# Revit family: 1000_Sliding_Window_XXXX_Standard
name_source: partatom
category: Windows
revit_build: Autodesk Revit 2014 (Build: 20130308_1515(x64)
units: mm (PartAtom-declared; Revit-internal decimal feet)

## types (72) — shared parameters
Centered In Wall = Yes
Custom Sash Width Side = 800 mm  [stored 2.62467 ft]
Default Sill Height = 800 mm  [stored 2.62467 ft]
Description = Sliding window, XXXX
Equal Sash Width = Yes
Frame Thickness = 76 mm
Heavy Duty Handle Gap = 26 mm
Limit Sash Height Max = 1800 mm  [stored 5.90551 ft]
Limit Sash Height Min = 300 mm  [stored 0.984252 ft]
Limit Sash Width Max = 1500 mm  [stored 4.92126 ft]
Limit Sash Width Min = 300 mm  [stored 0.984252 ft]
Limit Sash Width Side Min = 300 mm  [stored 0.984252 ft]
Limit Window Height Max = 1857 mm
Limit Window Height Min = 357 mm
Limit Window Width Max = 5941 mm  [stored 19.4915 ft]
Limit Window Width Min = 1141 mm  [stored 3.74344 ft]
Manufacturer = Crealco
Model = 1000
Sash Frame Seal = 2 mm  [stored 0.00656168 ft]
URL = http://www.crealco.co.za
Wall Closure = By host
zero-valued in all types: Custom Frame Offset From Exterior

## per-type parameters (varying)
- 1000SW-1806XXXX-1000Pa: Area Middle Sash Glazing=0.16 m²; Area Side Sash Glazing=0.16 m²; Clearvue SHGC Value=0.498; Clearvue U Value=6.41; Custom Windload=1000 mm  [stored 3.28084 ft]; Custom Window Height=590 mm  [stored 1.9357 ft]; Custom Window Width=1790 mm  [stored 5.8727 ft]; Energy Advantage SHGC Value=0.448; Energy Advantage U Value=5.39; Heavy Duty Handle=No; Heavy Duty Interlocker=No; Height=590 mm  [stored 1.9357 ft]; Intruderprufe LowE SHGC Value=0.415; Intruderprufe LowE U Value=5.34; Intruderprufe SHGC Value=0.474; Intruderprufe U Value=6.29; Is Heavy Duty Handle=0 mm  [stored 0 ft]; Is Heavy Duty Mullion=0 mm  [stored 0 ft]; Limit Sash Width Side Max=625 mm; Max Pane Area=0.16 m²; Sash Height=533 mm; Sash Width Middle=462 mm; Sash Width Sides=462 mm; Standard Interlocker=Yes; Width=1790 mm  [stored 5.8727 ft]; Windload Design=1000 mm  [stored 3.28084 ft]
- 1000SW-2106XXXX-1000Pa: Area Middle Sash Glazing=0.19 m²; Area Side Sash Glazing=0.19 m²; Clearvue SHGC Value=0.515; Clearvue U Value=6.4; Custom Windload=1000 mm  [stored 3.28084 ft]; Custom Window Height=590 mm  [stored 1.9357 ft]; Custom Window Width=2090 mm  [stored 6.85696 ft]; Energy Advantage SHGC Value=0.463; Energy Advantage U Value=5.31; Heavy Duty Handle=No; Heavy Duty Interlocker=No; Height=590 mm  [stored 1.9357 ft]; Intruderprufe LowE SHGC Value=0.428; Intruderprufe LowE U Value=5.26; Intruderprufe SHGC Value=0.49; Intruderprufe U Value=6.29; Is Heavy Duty Handle=0 mm  [stored 0 ft]; Is Heavy Duty Mullion=0 mm  [stored 0 ft]; Limit Sash Width Side Max=775 mm; Max Pane Area=0.19 m²; Sash Height=533 mm; Sash Width Middle=537 mm  [stored 1.76181 ft]; Sash Width Sides=537 mm  [stored 1.76181 ft]; Standard Interlocker=Yes; Width=2090 mm  [stored 6.85696 ft]; Windload Design=1000 mm  [stored 3.28084 ft]
- 1000SW-2406XXXX-1000Pa: Area Middle Sash Glazing=0.22 m²; Area Side Sash Glazing=0.22 m²; Clearvue SHGC Value=0.528; Clearvue U Value=6.39; Custom Windload=1000 mm  [stored 3.28084 ft]; Custom Window Height=590 mm  [stored 1.9357 ft]; Custom Window Width=2390 mm  [stored 7.84121 ft]; Energy Advantage SHGC Value=0.474; Energy Advantage U Value=5.25; Heavy Duty Handle=No; Heavy Duty Interlocker=No; Height=590 mm  [stored 1.9357 ft]; Intruderprufe LowE SHGC Value=0.438; Intruderprufe LowE U Value=5.21; Intruderprufe SHGC Value=0.627; Intruderprufe U Value=5.98; Is Heavy Duty Handle=0 mm  [stored 0 ft]; Is Heavy Duty Mullion=0 mm  [stored 0 ft]; Limit Sash Width Side Max=925 mm; Max Pane Area=0.22 m²; Sash Height=533 mm; Sash Width Middle=612 mm; Sash Width Sides=612 mm; Standard Interlocker=Yes; Width=2390 mm  [stored 7.84121 ft]; Windload Design=1000 mm  [stored 3.28084 ft]
- 1000SW-2706XXXX-1000Pa: Area Middle Sash Glazing=0.25 m²; Area Side Sash Glazing=0.25 m²; Clearvue SHGC Value=0.537; Clearvue U Value=6.39; Custom Windload=1000 mm  [stored 3.28084 ft]; Custom Window Height=590 mm  [stored 1.9357 ft]; Custom Window Width=2690 mm  [stored 8.82546 ft]; Energy Advantage SHGC Value=0.483; Energy Advantage U Value=5.21; Heavy Duty Handle=No; Heavy Duty Interlocker=No; Height=590 mm  [stored 1.9357 ft]; Intruderprufe LowE SHGC Value=0.446; Intruderprufe LowE U Value=5.16; Intruderprufe SHGC Value=0.511; Intruderprufe U Value=6.28; Is Heavy Duty Handle=0 mm  [stored 0 ft]; Is Heavy Duty Mullion=0 mm  [stored 0 ft]; Limit Sash Width Side Max=1075 mm; Max Pane Area=0.25 m²; Sash Height=533 mm; Sash Width Middle=687 mm; Sash Width Sides=687 mm; Standard Interlocker=Yes; Width=2690 mm  [stored 8.82546 ft]; Windload Design=1000 mm  [stored 3.28084 ft]
- 1000SW-3006XXXX-1000Pa: Area Middle Sash Glazing=0.29 m²; Area Side Sash Glazing=0.29 m²; Clearvue SHGC Value=0.545; Clearvue U Value=6.39; Custom Windload=1000 mm  [stored 3.28084 ft]; Custom Window Height=590 mm  [stored 1.9357 ft]; Custom Window Width=2990 mm  [stored 9.80971 ft]; Energy Advantage SHGC Value=0.489; Energy Advantage U Value=5.17; Heavy Duty Handle=No; Heavy Duty Interlocker=No; Height=590 mm  [stored 1.9357 ft]; Intruderprufe LowE SHGC Value=0.452; Intruderprufe LowE U Value=5.13; Intruderprufe SHGC Value=0.518; Intruderprufe U Value=6.27; Is Heavy Duty Handle=0 mm  [stored 0 ft]; Is Heavy Duty Mullion=0 mm  [stored 0 ft]; Limit Sash Width Side Max=1225 mm; Max Pane Area=0.29 m²; Sash Height=533 mm; Sash Width Middle=762 mm; Sash Width Sides=762 mm; Standard Interlocker=Yes; Width=2990 mm  [stored 9.80971 ft]; Windload Design=1000 mm  [stored 3.28084 ft]
- 1000SW-1809XXXX-1000Pa: Area Middle Sash Glazing=0.26 m²; Area Side Sash Glazing=0.26 m²; Clearvue SHGC Value=0.561; Clearvue U Value=6.26; Custom Windload=1000 mm  [stored 3.28084 ft]; Custom Window Height=890 mm  [stored 2.91995 ft]; Custom Window Width=1790 mm  [stored 5.8727 ft]; Energy Advantage SHGC Value=0.504; Energy Advantage U Value=5.11; Heavy Duty Handle=No; Heavy Duty Interlocker=No; Height=890 mm  [stored 2.91995 ft]; Intruderprufe LowE SHGC Value=0.468; Intruderprufe LowE U Value=5.05; Intruderprufe SHGC Value=0.534; Intruderprufe U Value=6.15; Is Heavy Duty Handle=0 mm  [stored 0 ft]; Is Heavy Duty Mullion=0 mm  [stored 0 ft]; Limit Sash Width Side Max=625 mm; Max Pane Area=0.26 m²; Sash Height=833 mm; Sash Width Middle=462 mm; Sash Width Sides=462 mm; Standard Interlocker=Yes; Width=1790 mm  [stored 5.8727 ft]; Windload Design=1000 mm  [stored 3.28084 ft]
- 1000SW-2109XXXX-1000Pa: Area Middle Sash Glazing=0.32 m²; Area Side Sash Glazing=0.32 m²; Clearvue SHGC Value=0.58; Clearvue U Value=6.25; Custom Windload=1000 mm  [stored 3.28084 ft]; Custom Window Height=890 mm  [stored 2.91995 ft]; Custom Window Width=2090 mm  [stored 6.85696 ft]; Energy Advantage SHGC Value=0.521; Energy Advantage U Value=5.02; Heavy Duty Handle=No; Heavy Duty Interlocker=No; Height=890 mm  [stored 2.91995 ft]; Intruderprufe LowE SHGC Value=0.483; Intruderprufe LowE U Value=4.96; Intruderprufe SHGC Value=0.552; Intruderprufe U Value=6.14; Is Heavy Duty Handle=0 mm  [stored 0 ft]; Is Heavy Duty Mullion=0 mm  [stored 0 ft]; Limit Sash Width Side Max=775 mm; Max Pane Area=0.32 m²; Sash Height=833 mm; Sash Width Middle=537 mm  [stored 1.76181 ft]; Sash Width Sides=537 mm  [stored 1.76181 ft]; Standard Interlocker=Yes; Width=2090 mm  [stored 6.85696 ft]; Windload Design=1000 mm  [stored 3.28084 ft]
- 1000SW-2409XXXX-1000Pa: Area Middle Sash Glazing=0.37 m²; Area Side Sash Glazing=0.37 m²; Clearvue SHGC Value=0.595; Clearvue U Value=6.25; Custom Windload=1000 mm  [stored 3.28084 ft]; Custom Window Height=890 mm  [stored 2.91995 ft]; Custom Window Width=2390 mm  [stored 7.84121 ft]; Energy Advantage SHGC Value=0.533; Energy Advantage U Value=4.95; Heavy Duty Handle=No; Heavy Duty Interlocker=No; Height=890 mm  [stored 2.91995 ft]; Intruderprufe LowE SHGC Value=0.494; Intruderprufe LowE U Value=4.89; Intruderprufe SHGC Value=0.565; Intruderprufe U Value=6.13; Is Heavy Duty Handle=0 mm  [stored 0 ft]; Is Heavy Duty Mullion=0 mm  [stored 0 ft]; Limit Sash Width Side Max=925 mm; Max Pane Area=0.37 m²; Sash Height=833 mm; Sash Width Middle=612 mm; Sash Width Sides=612 mm; Standard Interlocker=Yes; Width=2390 mm  [stored 7.84121 ft]; Windload Design=1000 mm  [stored 3.28084 ft]
- 1000SW-2709XXXX-1000Pa: Area Middle Sash Glazing=0.43 m²; Area Side Sash Glazing=0.43 m²; Clearvue SHGC Value=0.606; Clearvue U Value=6.24; Custom Windload=1000 mm  [stored 3.28084 ft]; Custom Window Height=890 mm  [stored 2.91995 ft]; Custom Window Width=2690 mm  [stored 8.82546 ft]; Energy Advantage SHGC Value=0.543; Energy Advantage U Value=4.89; Heavy Duty Handle=No; Heavy Duty Interlocker=No; Height=890 mm  [stored 2.91995 ft]; Intruderprufe LowE SHGC Value=0.503; Intruderprufe LowE U Value=4.84; Intruderprufe SHGC Value=0.576; Intruderprufe U Value=6.12; Is Heavy Duty Handle=0 mm  [stored 0 ft]; Is Heavy Duty Mullion=0 mm  [stored 0 ft]; Limit Sash Width Side Max=1075 mm; Max Pane Area=0.43 m²; Sash Height=833 mm; Sash Width Middle=687 mm; Sash Width Sides=687 mm; Standard Interlocker=Yes; Width=2690 mm  [stored 8.82546 ft]; Windload Design=1000 mm  [stored 3.28084 ft]
- 1000SW-3009XXXX-1000Pa: Area Middle Sash Glazing=0.48 m²; Area Side Sash Glazing=0.48 m²; Clearvue SHGC Value=0.615; Clearvue U Value=6.24; Custom Windload=1000 mm  [stored 3.28084 ft]; Custom Window Height=890 mm  [stored 2.91995 ft]; Custom Window Width=2990 mm  [stored 9.80971 ft]; Energy Advantage SHGC Value=0.551; Energy Advantage U Value=4.85; Heavy Duty Handle=No; Heavy Duty Interlocker=No; Height=890 mm  [stored 2.91995 ft]; Intruderprufe LowE SHGC Value=0.51; Intruderprufe LowE U Value=4.79; Intruderprufe SHGC Value=0.584; Intruderprufe U Value=6.12; Is Heavy Duty Handle=0 mm  [stored 0 ft]; Is Heavy Duty Mullion=0 mm  [stored 0 ft]; Limit Sash Width Side Max=1225 mm; Max Pane Area=0.48 m²; Sash Height=833 mm; Sash Width Middle=762 mm; Sash Width Sides=762 mm; Standard Interlocker=Yes; Width=2990 mm  [stored 9.80971 ft]; Windload Design=1000 mm  [stored 3.28084 ft]
- 1000SW-1812XXXX-1000Pa: Area Middle Sash Glazing=0.37 m²; Area Side Sash Glazing=0.37 m²; Clearvue SHGC Value=0.592; Clearvue U Value=6.19; Custom Windload=1000 mm  [stored 3.28084 ft]; Custom Window Height=1190 mm  [stored 3.9042 ft]; Custom Window Width=1790 mm  [stored 5.8727 ft]; Energy Advantage SHGC Value=0.531; Energy Advantage U Value=4.97; Heavy Duty Handle=No; Heavy Duty Interlocker=No; Height=1190 mm  [stored 3.9042 ft]; Intruderprufe LowE SHGC Value=0.494; Intruderprufe LowE U Value=4.91; Intruderprufe SHGC Value=0.563; Intruderprufe U Value=6.08; Is Heavy Duty Handle=0 mm  [stored 0 ft]; Is Heavy Duty Mullion=0 mm  [stored 0 ft]; Limit Sash Width Side Max=625 mm; Max Pane Area=0.37 m²; Sash Height=1133 mm; Sash Width Middle=462 mm; Sash Width Sides=462 mm; Standard Interlocker=Yes; Width=1790 mm  [stored 5.8727 ft]; Windload Design=1000 mm  [stored 3.28084 ft]
- 1000SW-2112XXXX-1000Pa: Area Middle Sash Glazing=0.45 m²; Area Side Sash Glazing=0.45 m²; Clearvue SHGC Value=0.612; Clearvue U Value=6.8; Custom Windload=1000 mm  [stored 3.28084 ft]; Custom Window Height=1190 mm  [stored 3.9042 ft]; Custom Window Width=2090 mm  [stored 6.85696 ft]; Energy Advantage SHGC Value=0.549; Energy Advantage U Value=4.87; Heavy Duty Handle=No; Heavy Duty Interlocker=No; Height=1190 mm  [stored 3.9042 ft]; Intruderprufe LowE SHGC Value=0.51; Intruderprufe LowE U Value=4.81; Intruderprufe SHGC Value=0.582; Intruderprufe U Value=6.07; Is Heavy Duty Handle=0 mm  [stored 0 ft]; Is Heavy Duty Mullion=0 mm  [stored 0 ft]; Limit Sash Width Side Max=775 mm; Max Pane Area=0.45 m²; Sash Height=1133 mm; Sash Width Middle=537 mm  [stored 1.76181 ft]; Sash Width Sides=537 mm  [stored 1.76181 ft]; Standard Interlocker=Yes; Width=2090 mm  [stored 6.85696 ft]; Windload Design=1000 mm  [stored 3.28084 ft]
- 1000SW-2412XXXX-1000Pa: Area Middle Sash Glazing=0.53 m²; Area Side Sash Glazing=0.53 m²; Clearvue SHGC Value=0.628; Clearvue U Value=6.17; Custom Windload=1000 mm  [stored 3.28084 ft]; Custom Window Height=1190 mm  [stored 3.9042 ft]; Custom Window Width=2390 mm  [stored 7.84121 ft]; Energy Advantage SHGC Value=0.562; Energy Advantage U Value=4.8; Heavy Duty Handle=No; Heavy Duty Interlocker=No; Height=1190 mm  [stored 3.9042 ft]; Intruderprufe LowE SHGC Value=0.522; Intruderprufe LowE U Value=4.73; Intruderprufe SHGC Value=0.596; Intruderprufe U Value=6.06; Is Heavy Duty Handle=0 mm  [stored 0 ft]; Is Heavy Duty Mullion=0 mm  [stored 0 ft]; Limit Sash Width Side Max=925 mm; Max Pane Area=0.53 m²; Sash Height=1133 mm; Sash Width Middle=612 mm; Sash Width Sides=612 mm; Standard Interlocker=Yes; Width=2390 mm  [stored 7.84121 ft]; Windload Design=1000 mm  [stored 3.28084 ft]
- 1000SW-2712XXXX-1000Pa: Area Middle Sash Glazing=0.61 m²; Area Side Sash Glazing=0.61 m²; Clearvue SHGC Value=0.64; Clearvue U Value=6.17; Custom Windload=1000 mm  [stored 3.28084 ft]; Custom Window Height=1190 mm  [stored 3.9042 ft]; Custom Window Width=2690 mm  [stored 8.82546 ft]; Energy Advantage SHGC Value=0.573; Energy Advantage U Value=4.74; Heavy Duty Handle=No; Heavy Duty Interlocker=No; Height=1190 mm  [stored 3.9042 ft]; Intruderprufe LowE SHGC Value=0.532; Intruderprufe LowE U Value=4.68; Intruderprufe SHGC Value=0.607; Intruderprufe U Value=6.05; Is Heavy Duty Handle=0 mm  [stored 0 ft]; Is Heavy Duty Mullion=0 mm  [stored 0 ft]; Limit Sash Width Side Max=1075 mm; Max Pane Area=0.61 m²; Sash Height=1133 mm; Sash Width Middle=687 mm; Sash Width Sides=687 mm; Standard Interlocker=Yes; Width=2690 mm  [stored 8.82546 ft]; Windload Design=1000 mm  [stored 3.28084 ft]
- 1000SW-3012XXXX-1000Pa: Area Middle Sash Glazing=0.68 m²; Area Side Sash Glazing=0.68 m²; Clearvue SHGC Value=0.649; Clearvue U Value=6.16; Custom Windload=1000 mm  [stored 3.28084 ft]; Custom Window Height=1190 mm  [stored 3.9042 ft]; Custom Window Width=2990 mm  [stored 9.80971 ft]; Energy Advantage SHGC Value=0.581; Energy Advantage U Value=4.69; Heavy Duty Handle=No; Heavy Duty Interlocker=No; Height=1190 mm  [stored 3.9042 ft]; Intruderprufe LowE SHGC Value=0.539; Intruderprufe LowE U Value=4.63; Intruderprufe SHGC Value=0.616; Intruderprufe U Value=6.04; Is Heavy Duty Handle=0 mm  [stored 0 ft]; Is Heavy Duty Mullion=0 mm  [stored 0 ft]; Limit Sash Width Side Max=1225 mm; Max Pane Area=0.68 m²; Sash Height=1133 mm; Sash Width Middle=762 mm; Sash Width Sides=762 mm; Standard Interlocker=Yes; Width=2990 mm  [stored 9.80971 ft]; Windload Design=1000 mm  [stored 3.28084 ft]
- 1000SW-1815XXXX-1000Pa: Area Middle Sash Glazing=0.48 m²; Area Side Sash Glazing=0.48 m²; Clearvue SHGC Value=0.611; Clearvue U Value=6.15; Custom Windload=1000 mm  [stored 3.28084 ft]; Custom Window Height=1490 mm  [stored 4.88845 ft]; Custom Window Width=1790 mm  [stored 5.8727 ft]; Energy Advantage SHGC Value=0.548; Energy Advantage U Value=4.89; Heavy Duty Handle=No; Heavy Duty Interlocker=No; Height=1490 mm  [stored 4.88845 ft]; Intruderprufe LowE SHGC Value=0.51; Intruderprufe LowE U Value=4.82; Intruderprufe SHGC Value=0.581; Intruderprufe U Value=6.03; Is Heavy Duty Handle=0 mm  [stored 0 ft]; Is Heavy Duty Mullion=0 mm  [stored 0 ft]; Limit Sash Width Side Max=625 mm; Max Pane Area=0.48 m²; Sash Height=1433 mm; Sash Width Middle=462 mm; Sash Width Sides=462 mm; Standard Interlocker=Yes; Width=1790 mm  [stored 5.8727 ft]; Windload Design=1000 mm  [stored 3.28084 ft]
- 1000SW-2115XXXX-1000Pa: Area Middle Sash Glazing=0.58 m²; Area Side Sash Glazing=0.58 m²; Clearvue SHGC Value=0.632; Clearvue U Value=6.14; Custom Windload=1000 mm  [stored 3.28084 ft]; Custom Window Height=1490 mm  [stored 4.88845 ft]; Custom Window Width=2090 mm  [stored 6.85696 ft]; Energy Advantage SHGC Value=0.566; Energy Advantage U Value=4.78; Heavy Duty Handle=No; Heavy Duty Interlocker=No; Height=1490 mm  [stored 4.88845 ft]; Intruderprufe LowE SHGC Value=0.526; Intruderprufe LowE U Value=4.72; Intruderprufe SHGC Value=0.6; Intruderprufe U Value=6.02; Is Heavy Duty Handle=0 mm  [stored 0 ft]; Is Heavy Duty Mullion=0 mm  [stored 0 ft]; Limit Sash Width Side Max=775 mm; Max Pane Area=0.58 m²; Sash Height=1433 mm; Sash Width Middle=537 mm  [stored 1.76181 ft]; Sash Width Sides=537 mm  [stored 1.76181 ft]; Standard Interlocker=Yes; Width=2090 mm  [stored 6.85696 ft]; Windload Design=1000 mm  [stored 3.28084 ft]
- 1000SW-2415XXXX-1000Pa: Area Middle Sash Glazing=0.68 m²; Area Side Sash Glazing=0.68 m²; Clearvue SHGC Value=0.647; Clearvue U Value=6.13; Custom Windload=1000 mm  [stored 3.28084 ft]; Custom Window Height=1490 mm  [stored 4.88845 ft]; Custom Window Width=2390 mm  [stored 7.84121 ft]; Energy Advantage SHGC Value=0.58; Energy Advantage U Value=4.71; Heavy Duty Handle=No; Heavy Duty Interlocker=No; Height=1490 mm  [stored 4.88845 ft]; Intruderprufe LowE SHGC Value=0.539; Intruderprufe LowE U Value=4.64; Intruderprufe SHGC Value=0.615; Intruderprufe U Value=6.01; Is Heavy Duty Handle=0 mm  [stored 0 ft]; Is Heavy Duty Mullion=0 mm  [stored 0 ft]; Limit Sash Width Side Max=925 mm; Max Pane Area=0.68 m²; Sash Height=1433 mm; Sash Width Middle=612 mm; Sash Width Sides=612 mm; Standard Interlocker=Yes; Width=2390 mm  [stored 7.84121 ft]; Windload Design=1000 mm  [stored 3.28084 ft]
- 1000SW-2715XXXX-1000Pa: Area Middle Sash Glazing=0.78 m²; Area Side Sash Glazing=0.78 m²; Clearvue SHGC Value=0.66; Clearvue U Value=6.12; Custom Windload=1000 mm  [stored 3.28084 ft]; Custom Window Height=1490 mm  [stored 4.88845 ft]; Custom Window Width=2690 mm  [stored 8.82546 ft]; Energy Advantage SHGC Value=0.591; Energy Advantage U Value=4.64; Heavy Duty Handle=No; Heavy Duty Interlocker=No; Height=1490 mm  [stored 4.88845 ft]; Intruderprufe LowE SHGC Value=0.549; Intruderprufe LowE U Value=4.58; Intruderprufe SHGC Value=0.627; Intruderprufe U Value=6; Is Heavy Duty Handle=0 mm  [stored 0 ft]; Is Heavy Duty Mullion=0 mm  [stored 0 ft]; Limit Sash Width Side Max=1075 mm; Max Pane Area=0.78 m²; Sash Height=1433 mm; Sash Width Middle=687 mm; Sash Width Sides=687 mm; Standard Interlocker=Yes; Width=2690 mm  [stored 8.82546 ft]; Windload Design=1000 mm  [stored 3.28084 ft]
- 1000SW-3015XXXX-1000Pa: Area Middle Sash Glazing=0.88 m²; Area Side Sash Glazing=0.88 m²; Clearvue SHGC Value=0.669; Clearvue U Value=6.12; Custom Windload=1000 mm  [stored 3.28084 ft]; Custom Window Height=1490 mm  [stored 4.88845 ft]; Custom Window Width=2990 mm  [stored 9.80971 ft]; Energy Advantage SHGC Value=0.599; Energy Advantage U Value=4.59; Heavy Duty Handle=No; Heavy Duty Interlocker=No; Height=1490 mm  [stored 4.88845 ft]; Intruderprufe LowE SHGC Value=0.557; Intruderprufe LowE U Value=4.53; Intruderprufe SHGC Value=0.636; Intruderprufe U Value=6; Is Heavy Duty Handle=0 mm  [stored 0 ft]; Is Heavy Duty Mullion=0 mm  [stored 0 ft]; Limit Sash Width Side Max=1225 mm; Max Pane Area=0.88 m²; Sash Height=1433 mm; Sash Width Middle=762 mm; Sash Width Sides=762 mm; Standard Interlocker=Yes; Width=2990 mm  [stored 9.80971 ft]; Windload Design=1000 mm  [stored 3.28084 ft]
- 1000SW-2118XXXX-1000Pa: Area Middle Sash Glazing=0.71 m²; Area Side Sash Glazing=0.71 m²; Clearvue SHGC Value=0.644; Clearvue U Value=6.11; Custom Windload=1000 mm  [stored 3.28084 ft]; Custom Window Height=1790 mm  [stored 5.8727 ft]; Custom Window Width=2090 mm  [stored 6.85696 ft]; Energy Advantage SHGC Value=0.577; Energy Advantage U Value=4.73; Heavy Duty Handle=Yes; Heavy Duty Interlocker=No; Height=1790 mm  [stored 5.8727 ft]; Intruderprufe LowE SHGC Value=0.537; Intruderprufe LowE U Value=4.66; Intruderprufe SHGC Value=0.612; Intruderprufe U Value=5.99; Is Heavy Duty Handle=1 mm  [stored 0.00328084 ft]; Is Heavy Duty Mullion=0 mm  [stored 0 ft]; Limit Sash Width Side Max=775 mm; Max Pane Area=0.71 m²; Sash Height=1733 mm; Sash Width Middle=537 mm  [stored 1.76181 ft]; Sash Width Sides=537 mm  [stored 1.76181 ft]; Standard Interlocker=Yes; Width=2090 mm  [stored 6.85696 ft]; Windload Design=1000 mm  [stored 3.28084 ft]
- 1000SW-2718XXXX-1000Pa: Area Middle Sash Glazing=0.96 m²; Area Side Sash Glazing=0.96 m²; Clearvue SHGC Value=0.673; Clearvue U Value=6.09; Custom Windload=1000 mm  [stored 3.28084 ft]; Custom Window Height=1790 mm  [stored 5.8727 ft]; Custom Window Width=2690 mm  [stored 8.82546 ft]; Energy Advantage SHGC Value=0.603; Energy Advantage U Value=4.58; Heavy Duty Handle=Yes; Heavy Duty Interlocker=Yes; Height=1790 mm  [stored 5.8727 ft]; Intruderprufe LowE SHGC Value=0.56; Intruderprufe LowE U Value=4.52; Intruderprufe SHGC Value=0.639; Intruderprufe U Value=5.97; Is Heavy Duty Handle=1 mm  [stored 0.00328084 ft]; Is Heavy Duty Mullion=1 mm  [stored 0.00328084 ft]; Limit Sash Width Side Max=1075 mm; Max Pane Area=0.96 m²; Sash Height=1733 mm; Sash Width Middle=687 mm; Sash Width Sides=687 mm; Standard Interlocker=No; Width=2690 mm  [stored 8.82546 ft]; Windload Design=1000 mm  [stored 3.28084 ft]
- 1000SW-3018XXXX-1000Pa: Area Middle Sash Glazing=1.08 m²; Area Side Sash Glazing=1.08 m²; Clearvue SHGC Value=0.683; Clearvue U Value=6.09; Custom Windload=1000 mm  [stored 3.28084 ft]; Custom Window Height=1790 mm  [stored 5.8727 ft]; Custom Window Width=2990 mm  [stored 9.80971 ft]; Energy Advantage SHGC Value=0.611; Energy Advantage U Value=4.53; Heavy Duty Handle=Yes; Heavy Duty Interlocker=Yes; Height=1790 mm  [stored 5.8727 ft]; Intruderprufe LowE SHGC Value=0.568; Intruderprufe LowE U Value=4.47; Intruderprufe SHGC Value=0.649; Intruderprufe U Value=5.97; Is Heavy Duty Handle=1 mm  [stored 0.00328084 ft]; Is Heavy Duty Mullion=1 mm  [stored 0.00328084 ft]; Limit Sash Width Side Max=1225 mm; Max Pane Area=1.08 m²; Sash Height=1733 mm; Sash Width Middle=762 mm; Sash Width Sides=762 mm; Standard Interlocker=No; Width=2990 mm  [stored 9.80971 ft]; Windload Design=1000 mm  [stored 3.28084 ft]
- 1000SW-2418XXXX-1000Pa: Area Middle Sash Glazing=0.83 m²; Area Side Sash Glazing=0.83 m²; Clearvue SHGC Value=0.661; Clearvue U Value=6.1; Custom Windload=1000 mm  [stored 3.28084 ft]; Custom Window Height=1790 mm  [stored 5.8727 ft]; Custom Window Width=2390 mm  [stored 7.84121 ft]; Energy Advantage SHGC Value=0.592; Energy Advantage U Value=4.64; Heavy Duty Handle=Yes; Heavy Duty Interlocker=No; Height=1790 mm  [stored 5.8727 ft]; Intruderprufe LowE SHGC Value=0.55; Intruderprufe LowE U Value=4.58; Intruderprufe SHGC Value=0.627; Intruderprufe U Value=5.98; Is Heavy Duty Handle=1 mm  [stored 0.00328084 ft]; Is Heavy Duty Mullion=0 mm  [stored 0 ft]; Limit Sash Width Side Max=925 mm; Max Pane Area=0.83 m²; Sash Height=1733 mm; Sash Width Middle=612 mm; Sash Width Sides=612 mm; Standard Interlocker=Yes; Width=2390 mm  [stored 7.84121 ft]; Windload Design=1000 mm  [stored 3.28084 ft]
- 1000SW-1806XXXX-1500Pa: Area Middle Sash Glazing=0.16 m²; Area Side Sash Glazing=0.16 m²; Clearvue SHGC Value=0.498; Clearvue U Value=6.41; Custom Windload=1500 mm  [stored 4.92126 ft]; Custom Window Height=590 mm  [stored 1.9357 ft]; Custom Window Width=1790 mm  [stored 5.8727 ft]; Energy Advantage SHGC Value=0.448; Energy Advantage U Value=5.39; Heavy Duty Handle=No; Heavy Duty Interlocker=No; Height=590 mm  [stored 1.9357 ft]; Intruderprufe LowE SHGC Value=0.415; Intruderprufe LowE U Value=5.34; Intruderprufe SHGC Value=0.474; Intruderprufe U Value=6.29; Is Heavy Duty Handle=0 mm  [stored 0 ft]; Is Heavy Duty Mullion=0 mm  [stored 0 ft]; Limit Sash Width Side Max=625 mm; Max Pane Area=0.16 m²; Sash Height=533 mm; Sash Width Middle=462 mm; Sash Width Sides=462 mm; Standard Interlocker=Yes; Width=1790 mm  [stored 5.8727 ft]; Windload Design=1500 mm  [stored 4.92126 ft]
- 1000SW-1806XXXX-2000Pa: Area Middle Sash Glazing=0.16 m²; Area Side Sash Glazing=0.16 m²; Clearvue SHGC Value=0.498; Clearvue U Value=6.41; Custom Windload=2000 mm  [stored 6.56168 ft]; Custom Window Height=590 mm  [stored 1.9357 ft]; Custom Window Width=1790 mm  [stored 5.8727 ft]; Energy Advantage SHGC Value=0.448; Energy Advantage U Value=5.39; Heavy Duty Handle=No; Heavy Duty Interlocker=No; Height=590 mm  [stored 1.9357 ft]; Intruderprufe LowE SHGC Value=0.415; Intruderprufe LowE U Value=5.34; Intruderprufe SHGC Value=0.474; Intruderprufe U Value=6.29; Is Heavy Duty Handle=0 mm  [stored 0 ft]; Is Heavy Duty Mullion=0 mm  [stored 0 ft]; Limit Sash Width Side Max=625 mm; Max Pane Area=0.16 m²; Sash Height=533 mm; Sash Width Middle=462 mm; Sash Width Sides=462 mm; Standard Interlocker=Yes; Width=1790 mm  [stored 5.8727 ft]; Windload Design=2000 mm  [stored 6.56168 ft]
- 1000SW-1809XXXX-1500Pa: Area Middle Sash Glazing=0.26 m²; Area Side Sash Glazing=0.26 m²; Clearvue SHGC Value=0.561; Clearvue U Value=6.26; Custom Windload=1500 mm  [stored 4.92126 ft]; Custom Window Height=890 mm  [stored 2.91995 ft]; Custom Window Width=1790 mm  [stored 5.8727 ft]; Energy Advantage SHGC Value=0.504; Energy Advantage U Value=5.11; Heavy Duty Handle=No; Heavy Duty Interlocker=No; Height=890 mm  [stored 2.91995 ft]; Intruderprufe LowE SHGC Value=0.468; Intruderprufe LowE U Value=5.05; Intruderprufe SHGC Value=0.534; Intruderprufe U Value=6.15; Is Heavy Duty Handle=0 mm  [stored 0 ft]; Is Heavy Duty Mullion=0 mm  [stored 0 ft]; Limit Sash Width Side Max=625 mm; Max Pane Area=0.26 m²; Sash Height=833 mm; Sash Width Middle=462 mm; Sash Width Sides=462 mm; Standard Interlocker=Yes; Width=1790 mm  [stored 5.8727 ft]; Windload Design=1500 mm  [stored 4.92126 ft]
- 1000SW-1809XXXX-2000Pa: Area Middle Sash Glazing=0.26 m²; Area Side Sash Glazing=0.26 m²; Clearvue SHGC Value=0.561; Clearvue U Value=6.26; Custom Windload=2000 mm  [stored 6.56168 ft]; Custom Window Height=890 mm  [stored 2.91995 ft]; Custom Window Width=1790 mm  [stored 5.8727 ft]; Energy Advantage SHGC Value=0.504; Energy Advantage U Value=5.11; Heavy Duty Handle=No; Heavy Duty Interlocker=No; Height=890 mm  [stored 2.91995 ft]; Intruderprufe LowE SHGC Value=0.468; Intruderprufe LowE U Value=5.05; Intruderprufe SHGC Value=0.534; Intruderprufe U Value=6.15; Is Heavy Duty Handle=0 mm  [stored 0 ft]; Is Heavy Duty Mullion=0 mm  [stored 0 ft]; Limit Sash Width Side Max=625 mm; Max Pane Area=0.26 m²; Sash Height=833 mm; Sash Width Middle=462 mm; Sash Width Sides=462 mm; Standard Interlocker=Yes; Width=1790 mm  [stored 5.8727 ft]; Windload Design=2000 mm  [stored 6.56168 ft]
- 1000SW-1812XXXX-1500Pa: Area Middle Sash Glazing=0.37 m²; Area Side Sash Glazing=0.37 m²; Clearvue SHGC Value=0.592; Clearvue U Value=6.19; Custom Windload=1500 mm  [stored 4.92126 ft]; Custom Window Height=1190 mm  [stored 3.9042 ft]; Custom Window Width=1790 mm  [stored 5.8727 ft]; Energy Advantage SHGC Value=0.531; Energy Advantage U Value=4.97; Heavy Duty Handle=No; Heavy Duty Interlocker=No; Height=1190 mm  [stored 3.9042 ft]; Intruderprufe LowE SHGC Value=0.494; Intruderprufe LowE U Value=4.91; Intruderprufe SHGC Value=0.563; Intruderprufe U Value=6.08; Is Heavy Duty Handle=0 mm  [stored 0 ft]; Is Heavy Duty Mullion=0 mm  [stored 0 ft]; Limit Sash Width Side Max=625 mm; Max Pane Area=0.37 m²; Sash Height=1133 mm; Sash Width Middle=462 mm; Sash Width Sides=462 mm; Standard Interlocker=Yes; Width=1790 mm  [stored 5.8727 ft]; Windload Design=1500 mm  [stored 4.92126 ft]
- 1000SW-1812XXXX-2000Pa: Area Middle Sash Glazing=0.37 m²; Area Side Sash Glazing=0.37 m²; Clearvue SHGC Value=0.592; Clearvue U Value=6.19; Custom Windload=2000 mm  [stored 6.56168 ft]; Custom Window Height=1190 mm  [stored 3.9042 ft]; Custom Window Width=1790 mm  [stored 5.8727 ft]; Energy Advantage SHGC Value=0.531; Energy Advantage U Value=4.97; Heavy Duty Handle=No; Heavy Duty Interlocker=No; Height=1190 mm  [stored 3.9042 ft]; Intruderprufe LowE SHGC Value=0.494; Intruderprufe LowE U Value=4.91; Intruderprufe SHGC Value=0.563; Intruderprufe U Value=6.08; Is Heavy Duty Handle=0 mm  [stored 0 ft]; Is Heavy Duty Mullion=0 mm  [stored 0 ft]; Limit Sash Width Side Max=625 mm; Max Pane Area=0.37 m²; Sash Height=1133 mm; Sash Width Middle=462 mm; Sash Width Sides=462 mm; Standard Interlocker=Yes; Width=1790 mm  [stored 5.8727 ft]; Windload Design=2000 mm  [stored 6.56168 ft]
- 1000SW-1815XXXX-1500Pa: Area Middle Sash Glazing=0.48 m²; Area Side Sash Glazing=0.48 m²; Clearvue SHGC Value=0.611; Clearvue U Value=6.15; Custom Windload=1500 mm  [stored 4.92126 ft]; Custom Window Height=1490 mm  [stored 4.88845 ft]; Custom Window Width=1790 mm  [stored 5.8727 ft]; Energy Advantage SHGC Value=0.548; Energy Advantage U Value=4.89; Heavy Duty Handle=No; Heavy Duty Interlocker=No; Height=1490 mm  [stored 4.88845 ft]; Intruderprufe LowE SHGC Value=0.51; Intruderprufe LowE U Value=4.82; Intruderprufe SHGC Value=0.581; Intruderprufe U Value=6.03; Is Heavy Duty Handle=0 mm  [stored 0 ft]; Is Heavy Duty Mullion=0 mm  [stored 0 ft]; Limit Sash Width Side Max=625 mm; Max Pane Area=0.48 m²; Sash Height=1433 mm; Sash Width Middle=462 mm; Sash Width Sides=462 mm; Standard Interlocker=Yes; Width=1790 mm  [stored 5.8727 ft]; Windload Design=1500 mm  [stored 4.92126 ft]
- 1000SW-1815XXXX-2000Pa: Area Middle Sash Glazing=0.48 m²; Area Side Sash Glazing=0.48 m²; Clearvue SHGC Value=0.611; Clearvue U Value=6.15; Custom Windload=2000 mm  [stored 6.56168 ft]; Custom Window Height=1490 mm  [stored 4.88845 ft]; Custom Window Width=1790 mm  [stored 5.8727 ft]; Energy Advantage SHGC Value=0.548; Energy Advantage U Value=4.89; Heavy Duty Handle=No; Heavy Duty Interlocker=No; Height=1490 mm  [stored 4.88845 ft]; Intruderprufe LowE SHGC Value=0.51; Intruderprufe LowE U Value=4.82; Intruderprufe SHGC Value=0.581; Intruderprufe U Value=6.03; Is Heavy Duty Handle=0 mm  [stored 0 ft]; Is Heavy Duty Mullion=0 mm  [stored 0 ft]; Limit Sash Width Side Max=625 mm; Max Pane Area=0.48 m²; Sash Height=1433 mm; Sash Width Middle=462 mm; Sash Width Sides=462 mm; Standard Interlocker=Yes; Width=1790 mm  [stored 5.8727 ft]; Windload Design=2000 mm  [stored 6.56168 ft]
- 1000SW-2106XXXX-1500Pa: Area Middle Sash Glazing=0.19 m²; Area Side Sash Glazing=0.19 m²; Clearvue SHGC Value=0.515; Clearvue U Value=6.4; Custom Windload=1500 mm  [stored 4.92126 ft]; Custom Window Height=590 mm  [stored 1.9357 ft]; Custom Window Width=2090 mm  [stored 6.85696 ft]; Energy Advantage SHGC Value=0.463; Energy Advantage U Value=5.31; Heavy Duty Handle=No; Heavy Duty Interlocker=No; Height=590 mm  [stored 1.9357 ft]; Intruderprufe LowE SHGC Value=0.428; Intruderprufe LowE U Value=5.26; Intruderprufe SHGC Value=0.49; Intruderprufe U Value=6.29; Is Heavy Duty Handle=0 mm  [stored 0 ft]; Is Heavy Duty Mullion=0 mm  [stored 0 ft]; Limit Sash Width Side Max=775 mm; Max Pane Area=0.19 m²; Sash Height=533 mm; Sash Width Middle=537 mm  [stored 1.76181 ft]; Sash Width Sides=537 mm  [stored 1.76181 ft]; Standard Interlocker=Yes; Width=2090 mm  [stored 6.85696 ft]; Windload Design=1500 mm  [stored 4.92126 ft]
- 1000SW-2106XXXX-2000Pa: Area Middle Sash Glazing=0.19 m²; Area Side Sash Glazing=0.19 m²; Clearvue SHGC Value=0.515; Clearvue U Value=6.4; Custom Windload=2000 mm  [stored 6.56168 ft]; Custom Window Height=590 mm  [stored 1.9357 ft]; Custom Window Width=2090 mm  [stored 6.85696 ft]; Energy Advantage SHGC Value=0.463; Energy Advantage U Value=5.31; Heavy Duty Handle=No; Heavy Duty Interlocker=No; Height=590 mm  [stored 1.9357 ft]; Intruderprufe LowE SHGC Value=0.428; Intruderprufe LowE U Value=5.26; Intruderprufe SHGC Value=0.49; Intruderprufe U Value=6.29; Is Heavy Duty Handle=0 mm  [stored 0 ft]; Is Heavy Duty Mullion=0 mm  [stored 0 ft]; Limit Sash Width Side Max=775 mm; Max Pane Area=0.19 m²; Sash Height=533 mm; Sash Width Middle=537 mm  [stored 1.76181 ft]; Sash Width Sides=537 mm  [stored 1.76181 ft]; Standard Interlocker=Yes; Width=2090 mm  [stored 6.85696 ft]; Windload Design=2000 mm  [stored 6.56168 ft]
- 1000SW-2109XXXX-1500Pa: Area Middle Sash Glazing=0.32 m²; Area Side Sash Glazing=0.32 m²; Clearvue SHGC Value=0.58; Clearvue U Value=6.25; Custom Windload=1500 mm  [stored 4.92126 ft]; Custom Window Height=890 mm  [stored 2.91995 ft]; Custom Window Width=2090 mm  [stored 6.85696 ft]; Energy Advantage SHGC Value=0.521; Energy Advantage U Value=5.02; Heavy Duty Handle=No; Heavy Duty Interlocker=No; Height=890 mm  [stored 2.91995 ft]; Intruderprufe LowE SHGC Value=0.483; Intruderprufe LowE U Value=4.96; Intruderprufe SHGC Value=0.552; Intruderprufe U Value=6.14; Is Heavy Duty Handle=0 mm  [stored 0 ft]; Is Heavy Duty Mullion=0 mm  [stored 0 ft]; Limit Sash Width Side Max=775 mm; Max Pane Area=0.32 m²; Sash Height=833 mm; Sash Width Middle=537 mm  [stored 1.76181 ft]; Sash Width Sides=537 mm  [stored 1.76181 ft]; Standard Interlocker=Yes; Width=2090 mm  [stored 6.85696 ft]; Windload Design=1500 mm  [stored 4.92126 ft]
- 1000SW-2109XXXX-2000Pa: Area Middle Sash Glazing=0.32 m²; Area Side Sash Glazing=0.32 m²; Clearvue SHGC Value=0.58; Clearvue U Value=6.25; Custom Windload=2000 mm  [stored 6.56168 ft]; Custom Window Height=890 mm  [stored 2.91995 ft]; Custom Window Width=2090 mm  [stored 6.85696 ft]; Energy Advantage SHGC Value=0.521; Energy Advantage U Value=5.02; Heavy Duty Handle=No; Heavy Duty Interlocker=No; Height=890 mm  [stored 2.91995 ft]; Intruderprufe LowE SHGC Value=0.483; Intruderprufe LowE U Value=4.96; Intruderprufe SHGC Value=0.552; Intruderprufe U Value=6.14; Is Heavy Duty Handle=0 mm  [stored 0 ft]; Is Heavy Duty Mullion=0 mm  [stored 0 ft]; Limit Sash Width Side Max=775 mm; Max Pane Area=0.32 m²; Sash Height=833 mm; Sash Width Middle=537 mm  [stored 1.76181 ft]; Sash Width Sides=537 mm  [stored 1.76181 ft]; Standard Interlocker=Yes; Width=2090 mm  [stored 6.85696 ft]; Windload Design=2000 mm  [stored 6.56168 ft]
- 1000SW-2112XXXX-2000Pa: Area Middle Sash Glazing=0.45 m²; Area Side Sash Glazing=0.45 m²; Clearvue SHGC Value=0.612; Clearvue U Value=6.8; Custom Windload=2000 mm  [stored 6.56168 ft]; Custom Window Height=1190 mm  [stored 3.9042 ft]; Custom Window Width=2090 mm  [stored 6.85696 ft]; Energy Advantage SHGC Value=0.549; Energy Advantage U Value=4.87; Heavy Duty Handle=No; Heavy Duty Interlocker=No; Height=1190 mm  [stored 3.9042 ft]; Intruderprufe LowE SHGC Value=0.51; Intruderprufe LowE U Value=4.81; Intruderprufe SHGC Value=0.582; Intruderprufe U Value=6.07; Is Heavy Duty Handle=0 mm  [stored 0 ft]; Is Heavy Duty Mullion=0 mm  [stored 0 ft]; Limit Sash Width Side Max=775 mm; Max Pane Area=0.45 m²; Sash Height=1133 mm; Sash Width Middle=537 mm  [stored 1.76181 ft]; Sash Width Sides=537 mm  [stored 1.76181 ft]; Standard Interlocker=Yes; Width=2090 mm  [stored 6.85696 ft]; Windload Design=2000 mm  [stored 6.56168 ft]
- 1000SW-2115XXXX-1500Pa: Area Middle Sash Glazing=0.58 m²; Area Side Sash Glazing=0.58 m²; Clearvue SHGC Value=0.632; Clearvue U Value=6.14; Custom Windload=1500 mm  [stored 4.92126 ft]; Custom Window Height=1490 mm  [stored 4.88845 ft]; Custom Window Width=2090 mm  [stored 6.85696 ft]; Energy Advantage SHGC Value=0.566; Energy Advantage U Value=4.78; Heavy Duty Handle=No; Heavy Duty Interlocker=No; Height=1490 mm  [stored 4.88845 ft]; Intruderprufe LowE SHGC Value=0.526; Intruderprufe LowE U Value=4.72; Intruderprufe SHGC Value=0.6; Intruderprufe U Value=6.02; Is Heavy Duty Handle=0 mm  [stored 0 ft]; Is Heavy Duty Mullion=0 mm  [stored 0 ft]; Limit Sash Width Side Max=775 mm; Max Pane Area=0.58 m²; Sash Height=1433 mm; Sash Width Middle=537 mm  [stored 1.76181 ft]; Sash Width Sides=537 mm  [stored 1.76181 ft]; Standard Interlocker=Yes; Width=2090 mm  [stored 6.85696 ft]; Windload Design=1500 mm  [stored 4.92126 ft]
- 1000SW-2115XXXX-2000Pa: Area Middle Sash Glazing=0.58 m²; Area Side Sash Glazing=0.58 m²; Clearvue SHGC Value=0.632; Clearvue U Value=6.14; Custom Windload=2000 mm  [stored 6.56168 ft]; Custom Window Height=1490 mm  [stored 4.88845 ft]; Custom Window Width=2090 mm  [stored 6.85696 ft]; Energy Advantage SHGC Value=0.566; Energy Advantage U Value=4.78; Heavy Duty Handle=Yes; Heavy Duty Interlocker=No; Height=1490 mm  [stored 4.88845 ft]; Intruderprufe LowE SHGC Value=0.526; Intruderprufe LowE U Value=4.72; Intruderprufe SHGC Value=0.6; Intruderprufe U Value=6.02; Is Heavy Duty Handle=1 mm  [stored 0.00328084 ft]; Is Heavy Duty Mullion=0 mm  [stored 0 ft]; Limit Sash Width Side Max=775 mm; Max Pane Area=0.58 m²; Sash Height=1433 mm; Sash Width Middle=537 mm  [stored 1.76181 ft]; Sash Width Sides=537 mm  [stored 1.76181 ft]; Standard Interlocker=Yes; Width=2090 mm  [stored 6.85696 ft]; Windload Design=2000 mm  [stored 6.56168 ft]
- 1000SW-2118XXXX-1500Pa: Area Middle Sash Glazing=0.71 m²; Area Side Sash Glazing=0.71 m²; Clearvue SHGC Value=0.644; Clearvue U Value=6.11; Custom Windload=1500 mm  [stored 4.92126 ft]; Custom Window Height=1790 mm  [stored 5.8727 ft]; Custom Window Width=2090 mm  [stored 6.85696 ft]; Energy Advantage SHGC Value=0.577; Energy Advantage U Value=4.73; Heavy Duty Handle=Yes; Heavy Duty Interlocker=Yes; Height=1790 mm  [stored 5.8727 ft]; Intruderprufe LowE SHGC Value=0.537; Intruderprufe LowE U Value=4.66; Intruderprufe SHGC Value=0.612; Intruderprufe U Value=5.99; Is Heavy Duty Handle=1 mm  [stored 0.00328084 ft]; Is Heavy Duty Mullion=1 mm  [stored 0.00328084 ft]; Limit Sash Width Side Max=775 mm; Max Pane Area=0.71 m²; Sash Height=1733 mm; Sash Width Middle=537 mm  [stored 1.76181 ft]; Sash Width Sides=537 mm  [stored 1.76181 ft]; Standard Interlocker=No; Width=2090 mm  [stored 6.85696 ft]; Windload Design=1500 mm  [stored 4.92126 ft]
- 1000SW-2118XXXX-2000Pa: Area Middle Sash Glazing=0.71 m²; Area Side Sash Glazing=0.71 m²; Clearvue SHGC Value=0.644; Clearvue U Value=6.11; Custom Windload=2000 mm  [stored 6.56168 ft]; Custom Window Height=1790 mm  [stored 5.8727 ft]; Custom Window Width=2090 mm  [stored 6.85696 ft]; Energy Advantage SHGC Value=0.577; Energy Advantage U Value=4.73; Heavy Duty Handle=Yes; Heavy Duty Interlocker=No; Height=1790 mm  [stored 5.8727 ft]; Intruderprufe LowE SHGC Value=0.537; Intruderprufe LowE U Value=4.66; Intruderprufe SHGC Value=0.612; Intruderprufe U Value=5.99; Is Heavy Duty Handle=1 mm  [stored 0.00328084 ft]; Is Heavy Duty Mullion=0 mm  [stored 0 ft]; Limit Sash Width Side Max=775 mm; Max Pane Area=0.71 m²; Sash Height=1733 mm; Sash Width Middle=537 mm  [stored 1.76181 ft]; Sash Width Sides=537 mm  [stored 1.76181 ft]; Standard Interlocker=Yes; Width=2090 mm  [stored 6.85696 ft]; Windload Design=2000 mm  [stored 6.56168 ft]
- 1000SW-2406XXXX-1500Pa: Area Middle Sash Glazing=0.22 m²; Area Side Sash Glazing=0.22 m²; Clearvue SHGC Value=0.528; Clearvue U Value=6.39; Custom Windload=1500 mm  [stored 4.92126 ft]; Custom Window Height=590 mm  [stored 1.9357 ft]; Custom Window Width=2390 mm  [stored 7.84121 ft]; Energy Advantage SHGC Value=0.474; Energy Advantage U Value=5.25; Heavy Duty Handle=No; Heavy Duty Interlocker=No; Height=590 mm  [stored 1.9357 ft]; Intruderprufe LowE SHGC Value=0.438; Intruderprufe LowE U Value=5.21; Intruderprufe SHGC Value=0.627; Intruderprufe U Value=5.98; Is Heavy Duty Handle=0 mm  [stored 0 ft]; Is Heavy Duty Mullion=0 mm  [stored 0 ft]; Limit Sash Width Side Max=925 mm; Max Pane Area=0.22 m²; Sash Height=533 mm; Sash Width Middle=612 mm; Sash Width Sides=612 mm; Standard Interlocker=Yes; Width=2390 mm  [stored 7.84121 ft]; Windload Design=1500 mm  [stored 4.92126 ft]
- 1000SW-2406XXXX-2000Pa: Area Middle Sash Glazing=0.22 m²; Area Side Sash Glazing=0.22 m²; Clearvue SHGC Value=0.528; Clearvue U Value=6.39; Custom Windload=2000 mm  [stored 6.56168 ft]; Custom Window Height=590 mm  [stored 1.9357 ft]; Custom Window Width=2390 mm  [stored 7.84121 ft]; Energy Advantage SHGC Value=0.474; Energy Advantage U Value=5.25; Heavy Duty Handle=No; Heavy Duty Interlocker=No; Height=590 mm  [stored 1.9357 ft]; Intruderprufe LowE SHGC Value=0.438; Intruderprufe LowE U Value=5.21; Intruderprufe SHGC Value=0.627; Intruderprufe U Value=5.98; Is Heavy Duty Handle=0 mm  [stored 0 ft]; Is Heavy Duty Mullion=0 mm  [stored 0 ft]; Limit Sash Width Side Max=925 mm; Max Pane Area=0.22 m²; Sash Height=533 mm; Sash Width Middle=612 mm; Sash Width Sides=612 mm; Standard Interlocker=Yes; Width=2390 mm  [stored 7.84121 ft]; Windload Design=2000 mm  [stored 6.56168 ft]
- 1000SW-2409XXXX-1500Pa: Area Middle Sash Glazing=0.37 m²; Area Side Sash Glazing=0.37 m²; Clearvue SHGC Value=0.595; Clearvue U Value=6.25; Custom Windload=1500 mm  [stored 4.92126 ft]; Custom Window Height=890 mm  [stored 2.91995 ft]; Custom Window Width=2390 mm  [stored 7.84121 ft]; Energy Advantage SHGC Value=0.533; Energy Advantage U Value=4.95; Heavy Duty Handle=No; Heavy Duty Interlocker=No; Height=890 mm  [stored 2.91995 ft]; Intruderprufe LowE SHGC Value=0.494; Intruderprufe LowE U Value=4.89; Intruderprufe SHGC Value=0.565; Intruderprufe U Value=6.13; Is Heavy Duty Handle=0 mm  [stored 0 ft]; Is Heavy Duty Mullion=0 mm  [stored 0 ft]; Limit Sash Width Side Max=925 mm; Max Pane Area=0.37 m²; Sash Height=833 mm; Sash Width Middle=612 mm; Sash Width Sides=612 mm; Standard Interlocker=Yes; Width=2390 mm  [stored 7.84121 ft]; Windload Design=1500 mm  [stored 4.92126 ft]
- 1000SW-2409XXXX-2000Pa: Area Middle Sash Glazing=0.37 m²; Area Side Sash Glazing=0.37 m²; Clearvue SHGC Value=0.595; Clearvue U Value=6.25; Custom Windload=2000 mm  [stored 6.56168 ft]; Custom Window Height=890 mm  [stored 2.91995 ft]; Custom Window Width=2390 mm  [stored 7.84121 ft]; Energy Advantage SHGC Value=0.533; Energy Advantage U Value=4.95; Heavy Duty Handle=No; Heavy Duty Interlocker=No; Height=890 mm  [stored 2.91995 ft]; Intruderprufe LowE SHGC Value=0.494; Intruderprufe LowE U Value=4.89; Intruderprufe SHGC Value=0.565; Intruderprufe U Value=6.13; Is Heavy Duty Handle=0 mm  [stored 0 ft]; Is Heavy Duty Mullion=0 mm  [stored 0 ft]; Limit Sash Width Side Max=925 mm; Max Pane Area=0.37 m²; Sash Height=833 mm; Sash Width Middle=612 mm; Sash Width Sides=612 mm; Standard Interlocker=Yes; Width=2390 mm  [stored 7.84121 ft]; Windload Design=2000 mm  [stored 6.56168 ft]
- 1000SW-2412XXXX-1500Pa: Area Middle Sash Glazing=0.53 m²; Area Side Sash Glazing=0.53 m²; Clearvue SHGC Value=0.628; Clearvue U Value=6.17; Custom Windload=1500 mm  [stored 4.92126 ft]; Custom Window Height=1190 mm  [stored 3.9042 ft]; Custom Window Width=2390 mm  [stored 7.84121 ft]; Energy Advantage SHGC Value=0.562; Energy Advantage U Value=4.8; Heavy Duty Handle=No; Heavy Duty Interlocker=No; Height=1190 mm  [stored 3.9042 ft]; Intruderprufe LowE SHGC Value=0.522; Intruderprufe LowE U Value=4.73; Intruderprufe SHGC Value=0.596; Intruderprufe U Value=6.06; Is Heavy Duty Handle=0 mm  [stored 0 ft]; Is Heavy Duty Mullion=0 mm  [stored 0 ft]; Limit Sash Width Side Max=925 mm; Max Pane Area=0.53 m²; Sash Height=1133 mm; Sash Width Middle=612 mm; Sash Width Sides=612 mm; Standard Interlocker=Yes; Width=2390 mm  [stored 7.84121 ft]; Windload Design=1500 mm  [stored 4.92126 ft]
- 1000SW-2412XXXX-2000Pa: Area Middle Sash Glazing=0.53 m²; Area Side Sash Glazing=0.53 m²; Clearvue SHGC Value=0.628; Clearvue U Value=6.17; Custom Windload=2000 mm  [stored 6.56168 ft]; Custom Window Height=1190 mm  [stored 3.9042 ft]; Custom Window Width=2390 mm  [stored 7.84121 ft]; Energy Advantage SHGC Value=0.562; Energy Advantage U Value=4.8; Heavy Duty Handle=No; Heavy Duty Interlocker=No; Height=1190 mm  [stored 3.9042 ft]; Intruderprufe LowE SHGC Value=0.522; Intruderprufe LowE U Value=4.73; Intruderprufe SHGC Value=0.596; Intruderprufe U Value=6.06; Is Heavy Duty Handle=0 mm  [stored 0 ft]; Is Heavy Duty Mullion=0 mm  [stored 0 ft]; Limit Sash Width Side Max=925 mm; Max Pane Area=0.53 m²; Sash Height=1133 mm; Sash Width Middle=612 mm; Sash Width Sides=612 mm; Standard Interlocker=Yes; Width=2390 mm  [stored 7.84121 ft]; Windload Design=2000 mm  [stored 6.56168 ft]
- 1000SW-2415XXXX-1500Pa: Area Middle Sash Glazing=0.68 m²; Area Side Sash Glazing=0.68 m²; Clearvue SHGC Value=0.647; Clearvue U Value=6.13; Custom Windload=1500 mm  [stored 4.92126 ft]; Custom Window Height=1490 mm  [stored 4.88845 ft]; Custom Window Width=2390 mm  [stored 7.84121 ft]; Energy Advantage SHGC Value=0.58; Energy Advantage U Value=4.71; Heavy Duty Handle=No; Heavy Duty Interlocker=No; Height=1490 mm  [stored 4.88845 ft]; Intruderprufe LowE SHGC Value=0.539; Intruderprufe LowE U Value=4.64; Intruderprufe SHGC Value=0.615; Intruderprufe U Value=6.01; Is Heavy Duty Handle=0 mm  [stored 0 ft]; Is Heavy Duty Mullion=0 mm  [stored 0 ft]; Limit Sash Width Side Max=925 mm; Max Pane Area=0.68 m²; Sash Height=1433 mm; Sash Width Middle=612 mm; Sash Width Sides=612 mm; Standard Interlocker=Yes; Width=2390 mm  [stored 7.84121 ft]; Windload Design=1500 mm  [stored 4.92126 ft]
- 1000SW-2415XXXX-2000Pa: Area Middle Sash Glazing=0.68 m²; Area Side Sash Glazing=0.68 m²; Clearvue SHGC Value=0.647; Clearvue U Value=6.13; Custom Windload=2000 mm  [stored 6.56168 ft]; Custom Window Height=1490 mm  [stored 4.88845 ft]; Custom Window Width=2390 mm  [stored 7.84121 ft]; Energy Advantage SHGC Value=0.58; Energy Advantage U Value=4.71; Heavy Duty Handle=Yes; Heavy Duty Interlocker=Yes; Height=1490 mm  [stored 4.88845 ft]; Intruderprufe LowE SHGC Value=0.539; Intruderprufe LowE U Value=4.64; Intruderprufe SHGC Value=0.615; Intruderprufe U Value=6.01; Is Heavy Duty Handle=1 mm  [stored 0.00328084 ft]; Is Heavy Duty Mullion=1 mm  [stored 0.00328084 ft]; Limit Sash Width Side Max=925 mm; Max Pane Area=0.68 m²; Sash Height=1433 mm; Sash Width Middle=612 mm; Sash Width Sides=612 mm; Standard Interlocker=No; Width=2390 mm  [stored 7.84121 ft]; Windload Design=2000 mm  [stored 6.56168 ft]
- 1000SW-2418XXXX-1500Pa: Area Middle Sash Glazing=0.83 m²; Area Side Sash Glazing=0.83 m²; Clearvue SHGC Value=0.661; Clearvue U Value=6.1; Custom Windload=1500 mm  [stored 4.92126 ft]; Custom Window Height=1790 mm  [stored 5.8727 ft]; Custom Window Width=2390 mm  [stored 7.84121 ft]; Energy Advantage SHGC Value=0.592; Energy Advantage U Value=4.64; Heavy Duty Handle=Yes; Heavy Duty Interlocker=Yes; Height=1790 mm  [stored 5.8727 ft]; Intruderprufe LowE SHGC Value=0.55; Intruderprufe LowE U Value=4.58; Intruderprufe SHGC Value=0.627; Intruderprufe U Value=5.98; Is Heavy Duty Handle=1 mm  [stored 0.00328084 ft]; Is Heavy Duty Mullion=1 mm  [stored 0.00328084 ft]; Limit Sash Width Side Max=925 mm; Max Pane Area=0.83 m²; Sash Height=1733 mm; Sash Width Middle=612 mm; Sash Width Sides=612 mm; Standard Interlocker=No; Width=2390 mm  [stored 7.84121 ft]; Windload Design=1500 mm  [stored 4.92126 ft]
- 1000SW-2418XXXX-2000Pa: Area Middle Sash Glazing=0.83 m²; Area Side Sash Glazing=0.83 m²; Clearvue SHGC Value=0.661; Clearvue U Value=6.1; Custom Windload=2000 mm  [stored 6.56168 ft]; Custom Window Height=1790 mm  [stored 5.8727 ft]; Custom Window Width=2390 mm  [stored 7.84121 ft]; Energy Advantage SHGC Value=0.592; Energy Advantage U Value=4.64; Heavy Duty Handle=Yes; Heavy Duty Interlocker=Yes; Height=1790 mm  [stored 5.8727 ft]; Intruderprufe LowE SHGC Value=0.55; Intruderprufe LowE U Value=4.58; Intruderprufe SHGC Value=0.627; Intruderprufe U Value=5.98; Is Heavy Duty Handle=1 mm  [stored 0.00328084 ft]; Is Heavy Duty Mullion=1 mm  [stored 0.00328084 ft]; Limit Sash Width Side Max=925 mm; Max Pane Area=0.83 m²; Sash Height=1733 mm; Sash Width Middle=612 mm; Sash Width Sides=612 mm; Standard Interlocker=No; Width=2390 mm  [stored 7.84121 ft]; Windload Design=2000 mm  [stored 6.56168 ft]
- 1000SW-2706XXXX-1500Pa: Area Middle Sash Glazing=0.25 m²; Area Side Sash Glazing=0.25 m²; Clearvue SHGC Value=0.537; Clearvue U Value=6.39; Custom Windload=1500 mm  [stored 4.92126 ft]; Custom Window Height=590 mm  [stored 1.9357 ft]; Custom Window Width=2690 mm  [stored 8.82546 ft]; Energy Advantage SHGC Value=0.483; Energy Advantage U Value=5.21; Heavy Duty Handle=No; Heavy Duty Interlocker=No; Height=590 mm  [stored 1.9357 ft]; Intruderprufe LowE SHGC Value=0.446; Intruderprufe LowE U Value=5.16; Intruderprufe SHGC Value=0.511; Intruderprufe U Value=6.28; Is Heavy Duty Handle=0 mm  [stored 0 ft]; Is Heavy Duty Mullion=0 mm  [stored 0 ft]; Limit Sash Width Side Max=1075 mm; Max Pane Area=0.25 m²; Sash Height=533 mm; Sash Width Middle=687 mm; Sash Width Sides=687 mm; Standard Interlocker=Yes; Width=2690 mm  [stored 8.82546 ft]; Windload Design=1500 mm  [stored 4.92126 ft]
- 1000SW-2706XXXX-2000Pa: Area Middle Sash Glazing=0.25 m²; Area Side Sash Glazing=0.25 m²; Clearvue SHGC Value=0.537; Clearvue U Value=6.39; Custom Windload=2000 mm  [stored 6.56168 ft]; Custom Window Height=590 mm  [stored 1.9357 ft]; Custom Window Width=2690 mm  [stored 8.82546 ft]; Energy Advantage SHGC Value=0.483; Energy Advantage U Value=5.21; Heavy Duty Handle=No; Heavy Duty Interlocker=No; Height=590 mm  [stored 1.9357 ft]; Intruderprufe LowE SHGC Value=0.446; Intruderprufe LowE U Value=5.16; Intruderprufe SHGC Value=0.511; Intruderprufe U Value=6.28; Is Heavy Duty Handle=0 mm  [stored 0 ft]; Is Heavy Duty Mullion=0 mm  [stored 0 ft]; Limit Sash Width Side Max=1075 mm; Max Pane Area=0.25 m²; Sash Height=533 mm; Sash Width Middle=687 mm; Sash Width Sides=687 mm; Standard Interlocker=Yes; Width=2690 mm  [stored 8.82546 ft]; Windload Design=2000 mm  [stored 6.56168 ft]
- 1000SW-2709XXXX-1500Pa: Area Middle Sash Glazing=0.43 m²; Area Side Sash Glazing=0.43 m²; Clearvue SHGC Value=0.606; Clearvue U Value=6.24; Custom Windload=1500 mm  [stored 4.92126 ft]; Custom Window Height=890 mm  [stored 2.91995 ft]; Custom Window Width=2690 mm  [stored 8.82546 ft]; Energy Advantage SHGC Value=0.543; Energy Advantage U Value=4.89; Heavy Duty Handle=No; Heavy Duty Interlocker=No; Height=890 mm  [stored 2.91995 ft]; Intruderprufe LowE SHGC Value=0.503; Intruderprufe LowE U Value=4.84; Intruderprufe SHGC Value=0.576; Intruderprufe U Value=6.12; Is Heavy Duty Handle=0 mm  [stored 0 ft]; Is Heavy Duty Mullion=0 mm  [stored 0 ft]; Limit Sash Width Side Max=1075 mm; Max Pane Area=0.43 m²; Sash Height=833 mm; Sash Width Middle=687 mm; Sash Width Sides=687 mm; Standard Interlocker=Yes; Width=2690 mm  [stored 8.82546 ft]; Windload Design=1500 mm  [stored 4.92126 ft]
- 1000SW-2709XXXX-2000Pa: Area Middle Sash Glazing=0.43 m²; Area Side Sash Glazing=0.43 m²; Clearvue SHGC Value=0.606; Clearvue U Value=6.24; Custom Windload=2000 mm  [stored 6.56168 ft]; Custom Window Height=890 mm  [stored 2.91995 ft]; Custom Window Width=2690 mm  [stored 8.82546 ft]; Energy Advantage SHGC Value=0.543; Energy Advantage U Value=4.89; Heavy Duty Handle=No; Heavy Duty Interlocker=No; Height=890 mm  [stored 2.91995 ft]; Intruderprufe LowE SHGC Value=0.503; Intruderprufe LowE U Value=4.84; Intruderprufe SHGC Value=0.576; Intruderprufe U Value=6.12; Is Heavy Duty Handle=0 mm  [stored 0 ft]; Is Heavy Duty Mullion=0 mm  [stored 0 ft]; Limit Sash Width Side Max=1075 mm; Max Pane Area=0.43 m²; Sash Height=833 mm; Sash Width Middle=687 mm; Sash Width Sides=687 mm; Standard Interlocker=Yes; Width=2690 mm  [stored 8.82546 ft]; Windload Design=2000 mm  [stored 6.56168 ft]
- 1000SW-2712XXXX-1500Pa: Area Middle Sash Glazing=0.61 m²; Area Side Sash Glazing=0.61 m²; Clearvue SHGC Value=0.64; Clearvue U Value=6.17; Custom Windload=1500 mm  [stored 4.92126 ft]; Custom Window Height=1190 mm  [stored 3.9042 ft]; Custom Window Width=2690 mm  [stored 8.82546 ft]; Energy Advantage SHGC Value=0.573; Energy Advantage U Value=4.74; Heavy Duty Handle=No; Heavy Duty Interlocker=No; Height=1190 mm  [stored 3.9042 ft]; Intruderprufe LowE SHGC Value=0.532; Intruderprufe LowE U Value=4.68; Intruderprufe SHGC Value=0.607; Intruderprufe U Value=6.05; Is Heavy Duty Handle=0 mm  [stored 0 ft]; Is Heavy Duty Mullion=0 mm  [stored 0 ft]; Limit Sash Width Side Max=1075 mm; Max Pane Area=0.61 m²; Sash Height=1133 mm; Sash Width Middle=687 mm; Sash Width Sides=687 mm; Standard Interlocker=Yes; Width=2690 mm  [stored 8.82546 ft]; Windload Design=1500 mm  [stored 4.92126 ft]
- 1000SW-2712XXXX-2000Pa: Area Middle Sash Glazing=0.61 m²; Area Side Sash Glazing=0.61 m²; Clearvue SHGC Value=0.64; Clearvue U Value=6.17; Custom Windload=2000 mm  [stored 6.56168 ft]; Custom Window Height=1190 mm  [stored 3.9042 ft]; Custom Window Width=2690 mm  [stored 8.82546 ft]; Energy Advantage SHGC Value=0.573; Energy Advantage U Value=4.74; Heavy Duty Handle=No; Heavy Duty Interlocker=No; Height=1190 mm  [stored 3.9042 ft]; Intruderprufe LowE SHGC Value=0.532; Intruderprufe LowE U Value=4.68; Intruderprufe SHGC Value=0.607; Intruderprufe U Value=6.05; Is Heavy Duty Handle=0 mm  [stored 0 ft]; Is Heavy Duty Mullion=0 mm  [stored 0 ft]; Limit Sash Width Side Max=1075 mm; Max Pane Area=0.61 m²; Sash Height=1133 mm; Sash Width Middle=687 mm; Sash Width Sides=687 mm; Standard Interlocker=Yes; Width=2690 mm  [stored 8.82546 ft]; Windload Design=2000 mm  [stored 6.56168 ft]
- 1000SW-2715XXXX-1500Pa: Area Middle Sash Glazing=0.78 m²; Area Side Sash Glazing=0.78 m²; Clearvue SHGC Value=0.66; Clearvue U Value=6.12; Custom Windload=1500 mm  [stored 4.92126 ft]; Custom Window Height=1490 mm  [stored 4.88845 ft]; Custom Window Width=2690 mm  [stored 8.82546 ft]; Energy Advantage SHGC Value=0.591; Energy Advantage U Value=4.64; Heavy Duty Handle=Yes; Heavy Duty Interlocker=No; Height=1490 mm  [stored 4.88845 ft]; Intruderprufe LowE SHGC Value=0.549; Intruderprufe LowE U Value=4.58; Intruderprufe SHGC Value=0.627; Intruderprufe U Value=6; Is Heavy Duty Handle=1 mm  [stored 0.00328084 ft]; Is Heavy Duty Mullion=0 mm  [stored 0 ft]; Limit Sash Width Side Max=1075 mm; Max Pane Area=0.78 m²; Sash Height=1433 mm; Sash Width Middle=687 mm; Sash Width Sides=687 mm; Standard Interlocker=Yes; Width=2690 mm  [stored 8.82546 ft]; Windload Design=1500 mm  [stored 4.92126 ft]
- 1000SW-2715XXXX-2000Pa: Area Middle Sash Glazing=0.78 m²; Area Side Sash Glazing=0.78 m²; Clearvue SHGC Value=0.66; Clearvue U Value=6.12; Custom Windload=2000 mm  [stored 6.56168 ft]; Custom Window Height=1490 mm  [stored 4.88845 ft]; Custom Window Width=2690 mm  [stored 8.82546 ft]; Energy Advantage SHGC Value=0.591; Energy Advantage U Value=4.64; Heavy Duty Handle=Yes; Heavy Duty Interlocker=Yes; Height=1490 mm  [stored 4.88845 ft]; Intruderprufe LowE SHGC Value=0.549; Intruderprufe LowE U Value=4.58; Intruderprufe SHGC Value=0.627; Intruderprufe U Value=6; Is Heavy Duty Handle=1 mm  [stored 0.00328084 ft]; Is Heavy Duty Mullion=1 mm  [stored 0.00328084 ft]; Limit Sash Width Side Max=1075 mm; Max Pane Area=0.78 m²; Sash Height=1433 mm; Sash Width Middle=687 mm; Sash Width Sides=687 mm; Standard Interlocker=No; Width=2690 mm  [stored 8.82546 ft]; Windload Design=2000 mm  [stored 6.56168 ft]
- 1000SW-2718XXXX-1500Pa: Area Middle Sash Glazing=0.96 m²; Area Side Sash Glazing=0.96 m²; Clearvue SHGC Value=0.673; Clearvue U Value=6.09; Custom Windload=1500 mm  [stored 4.92126 ft]; Custom Window Height=1790 mm  [stored 5.8727 ft]; Custom Window Width=2690 mm  [stored 8.82546 ft]; Energy Advantage SHGC Value=0.603; Energy Advantage U Value=4.58; Heavy Duty Handle=Yes; Heavy Duty Interlocker=Yes; Height=1790 mm  [stored 5.8727 ft]; Intruderprufe LowE SHGC Value=0.56; Intruderprufe LowE U Value=4.52; Intruderprufe SHGC Value=0.639; Intruderprufe U Value=5.97; Is Heavy Duty Handle=1 mm  [stored 0.00328084 ft]; Is Heavy Duty Mullion=1 mm  [stored 0.00328084 ft]; Limit Sash Width Side Max=1075 mm; Max Pane Area=0.96 m²; Sash Height=1733 mm; Sash Width Middle=687 mm; Sash Width Sides=687 mm; Standard Interlocker=No; Width=2690 mm  [stored 8.82546 ft]; Windload Design=1500 mm  [stored 4.92126 ft]
- 1000SW-2718XXXX-2000Pa: Area Middle Sash Glazing=0.96 m²; Area Side Sash Glazing=0.96 m²; Clearvue SHGC Value=0.673; Clearvue U Value=6.09; Custom Windload=2000 mm  [stored 6.56168 ft]; Custom Window Height=1790 mm  [stored 5.8727 ft]; Custom Window Width=2690 mm  [stored 8.82546 ft]; Energy Advantage SHGC Value=0.603; Energy Advantage U Value=4.58; Heavy Duty Handle=Yes; Heavy Duty Interlocker=Yes; Height=1790 mm  [stored 5.8727 ft]; Intruderprufe LowE SHGC Value=0.56; Intruderprufe LowE U Value=4.52; Intruderprufe SHGC Value=0.639; Intruderprufe U Value=5.97; Is Heavy Duty Handle=1 mm  [stored 0.00328084 ft]; Is Heavy Duty Mullion=1 mm  [stored 0.00328084 ft]; Limit Sash Width Side Max=1075 mm; Max Pane Area=0.96 m²; Sash Height=1733 mm; Sash Width Middle=687 mm; Sash Width Sides=687 mm; Standard Interlocker=No; Width=2690 mm  [stored 8.82546 ft]; Windload Design=2000 mm  [stored 6.56168 ft]
- 1000SW-3006XXXX-1500Pa: Area Middle Sash Glazing=0.29 m²; Area Side Sash Glazing=0.29 m²; Clearvue SHGC Value=0.545; Clearvue U Value=6.39; Custom Windload=1500 mm  [stored 4.92126 ft]; Custom Window Height=590 mm  [stored 1.9357 ft]; Custom Window Width=2990 mm  [stored 9.80971 ft]; Energy Advantage SHGC Value=0.489; Energy Advantage U Value=5.17; Heavy Duty Handle=No; Heavy Duty Interlocker=No; Height=590 mm  [stored 1.9357 ft]; Intruderprufe LowE SHGC Value=0.452; Intruderprufe LowE U Value=5.13; Intruderprufe SHGC Value=0.518; Intruderprufe U Value=6.27; Is Heavy Duty Handle=0 mm  [stored 0 ft]; Is Heavy Duty Mullion=0 mm  [stored 0 ft]; Limit Sash Width Side Max=1225 mm; Max Pane Area=0.29 m²; Sash Height=533 mm; Sash Width Middle=762 mm; Sash Width Sides=762 mm; Standard Interlocker=Yes; Width=2990 mm  [stored 9.80971 ft]; Windload Design=1500 mm  [stored 4.92126 ft]
- 1000SW-3006XXXX-2000Pa: Area Middle Sash Glazing=0.29 m²; Area Side Sash Glazing=0.29 m²; Clearvue SHGC Value=0.545; Clearvue U Value=6.39; Custom Windload=2000 mm  [stored 6.56168 ft]; Custom Window Height=590 mm  [stored 1.9357 ft]; Custom Window Width=2990 mm  [stored 9.80971 ft]; Energy Advantage SHGC Value=0.489; Energy Advantage U Value=5.17; Heavy Duty Handle=No; Heavy Duty Interlocker=No; Height=590 mm  [stored 1.9357 ft]; Intruderprufe LowE SHGC Value=0.452; Intruderprufe LowE U Value=5.13; Intruderprufe SHGC Value=0.518; Intruderprufe U Value=6.27; Is Heavy Duty Handle=0 mm  [stored 0 ft]; Is Heavy Duty Mullion=0 mm  [stored 0 ft]; Limit Sash Width Side Max=1225 mm; Max Pane Area=0.29 m²; Sash Height=533 mm; Sash Width Middle=762 mm; Sash Width Sides=762 mm; Standard Interlocker=Yes; Width=2990 mm  [stored 9.80971 ft]; Windload Design=2000 mm  [stored 6.56168 ft]
- 1000SW-3009XXXX-1500Pa: Area Middle Sash Glazing=0.48 m²; Area Side Sash Glazing=0.48 m²; Clearvue SHGC Value=0.615; Clearvue U Value=6.24; Custom Windload=1500 mm  [stored 4.92126 ft]; Custom Window Height=890 mm  [stored 2.91995 ft]; Custom Window Width=2990 mm  [stored 9.80971 ft]; Energy Advantage SHGC Value=0.551; Energy Advantage U Value=4.85; Heavy Duty Handle=No; Heavy Duty Interlocker=No; Height=890 mm  [stored 2.91995 ft]; Intruderprufe LowE SHGC Value=0.51; Intruderprufe LowE U Value=4.79; Intruderprufe SHGC Value=0.584; Intruderprufe U Value=6.12; Is Heavy Duty Handle=0 mm  [stored 0 ft]; Is Heavy Duty Mullion=0 mm  [stored 0 ft]; Limit Sash Width Side Max=1225 mm; Max Pane Area=0.48 m²; Sash Height=833 mm; Sash Width Middle=762 mm; Sash Width Sides=762 mm; Standard Interlocker=Yes; Width=2990 mm  [stored 9.80971 ft]; Windload Design=1500 mm  [stored 4.92126 ft]
- 1000SW-3009XXXX-2000Pa: Area Middle Sash Glazing=0.48 m²; Area Side Sash Glazing=0.48 m²; Clearvue SHGC Value=0.615; Clearvue U Value=6.24; Custom Windload=2000 mm  [stored 6.56168 ft]; Custom Window Height=890 mm  [stored 2.91995 ft]; Custom Window Width=2990 mm  [stored 9.80971 ft]; Energy Advantage SHGC Value=0.551; Energy Advantage U Value=4.85; Heavy Duty Handle=No; Heavy Duty Interlocker=No; Height=890 mm  [stored 2.91995 ft]; Intruderprufe LowE SHGC Value=0.51; Intruderprufe LowE U Value=4.79; Intruderprufe SHGC Value=0.584; Intruderprufe U Value=6.12; Is Heavy Duty Handle=0 mm  [stored 0 ft]; Is Heavy Duty Mullion=0 mm  [stored 0 ft]; Limit Sash Width Side Max=1225 mm; Max Pane Area=0.48 m²; Sash Height=833 mm; Sash Width Middle=762 mm; Sash Width Sides=762 mm; Standard Interlocker=Yes; Width=2990 mm  [stored 9.80971 ft]; Windload Design=2000 mm  [stored 6.56168 ft]
- 1000SW-3012XXXX-1500Pa: Area Middle Sash Glazing=0.68 m²; Area Side Sash Glazing=0.68 m²; Clearvue SHGC Value=0.649; Clearvue U Value=6.16; Custom Windload=1500 mm  [stored 4.92126 ft]; Custom Window Height=1190 mm  [stored 3.9042 ft]; Custom Window Width=2990 mm  [stored 9.80971 ft]; Energy Advantage SHGC Value=0.581; Energy Advantage U Value=4.69; Heavy Duty Handle=No; Heavy Duty Interlocker=No; Height=1190 mm  [stored 3.9042 ft]; Intruderprufe LowE SHGC Value=0.539; Intruderprufe LowE U Value=4.63; Intruderprufe SHGC Value=0.616; Intruderprufe U Value=6.04; Is Heavy Duty Handle=0 mm  [stored 0 ft]; Is Heavy Duty Mullion=0 mm  [stored 0 ft]; Limit Sash Width Side Max=1225 mm; Max Pane Area=0.68 m²; Sash Height=1133 mm; Sash Width Middle=762 mm; Sash Width Sides=762 mm; Standard Interlocker=Yes; Width=2990 mm  [stored 9.80971 ft]; Windload Design=1500 mm  [stored 4.92126 ft]
- 1000SW-3012XXXX-2000Pa: Area Middle Sash Glazing=0.68 m²; Area Side Sash Glazing=0.68 m²; Clearvue SHGC Value=0.649; Clearvue U Value=6.16; Custom Windload=2000 mm  [stored 6.56168 ft]; Custom Window Height=1190 mm  [stored 3.9042 ft]; Custom Window Width=2990 mm  [stored 9.80971 ft]; Energy Advantage SHGC Value=0.581; Energy Advantage U Value=4.69; Heavy Duty Handle=No; Heavy Duty Interlocker=No; Height=1190 mm  [stored 3.9042 ft]; Intruderprufe LowE SHGC Value=0.539; Intruderprufe LowE U Value=4.63; Intruderprufe SHGC Value=0.616; Intruderprufe U Value=6.04; Is Heavy Duty Handle=0 mm  [stored 0 ft]; Is Heavy Duty Mullion=0 mm  [stored 0 ft]; Limit Sash Width Side Max=1225 mm; Max Pane Area=0.68 m²; Sash Height=1133 mm; Sash Width Middle=762 mm; Sash Width Sides=762 mm; Standard Interlocker=Yes; Width=2990 mm  [stored 9.80971 ft]; Windload Design=2000 mm  [stored 6.56168 ft]
- 1000SW-3015XXXX-1500Pa: Area Middle Sash Glazing=0.88 m²; Area Side Sash Glazing=0.88 m²; Clearvue SHGC Value=0.669; Clearvue U Value=6.12; Custom Windload=1500 mm  [stored 4.92126 ft]; Custom Window Height=1490 mm  [stored 4.88845 ft]; Custom Window Width=2990 mm  [stored 9.80971 ft]; Energy Advantage SHGC Value=0.599; Energy Advantage U Value=4.59; Heavy Duty Handle=Yes; Heavy Duty Interlocker=No; Height=1490 mm  [stored 4.88845 ft]; Intruderprufe LowE SHGC Value=0.557; Intruderprufe LowE U Value=4.53; Intruderprufe SHGC Value=0.636; Intruderprufe U Value=6; Is Heavy Duty Handle=1 mm  [stored 0.00328084 ft]; Is Heavy Duty Mullion=0 mm  [stored 0 ft]; Limit Sash Width Side Max=1225 mm; Max Pane Area=0.88 m²; Sash Height=1433 mm; Sash Width Middle=762 mm; Sash Width Sides=762 mm; Standard Interlocker=Yes; Width=2990 mm  [stored 9.80971 ft]; Windload Design=1500 mm  [stored 4.92126 ft]
- 1000SW-3015XXXX-2000Pa: Area Middle Sash Glazing=0.88 m²; Area Side Sash Glazing=0.88 m²; Clearvue SHGC Value=0.669; Clearvue U Value=6.12; Custom Windload=2000 mm  [stored 6.56168 ft]; Custom Window Height=1490 mm  [stored 4.88845 ft]; Custom Window Width=2990 mm  [stored 9.80971 ft]; Energy Advantage SHGC Value=0.599; Energy Advantage U Value=4.59; Heavy Duty Handle=Yes; Heavy Duty Interlocker=Yes; Height=1490 mm  [stored 4.88845 ft]; Intruderprufe LowE SHGC Value=0.557; Intruderprufe LowE U Value=4.53; Intruderprufe SHGC Value=0.636; Intruderprufe U Value=6; Is Heavy Duty Handle=1 mm  [stored 0.00328084 ft]; Is Heavy Duty Mullion=1 mm  [stored 0.00328084 ft]; Limit Sash Width Side Max=1225 mm; Max Pane Area=0.88 m²; Sash Height=1433 mm; Sash Width Middle=762 mm; Sash Width Sides=762 mm; Standard Interlocker=No; Width=2990 mm  [stored 9.80971 ft]; Windload Design=2000 mm  [stored 6.56168 ft]
- 1000SW-3018XXXX-1500Pa: Area Middle Sash Glazing=1.08 m²; Area Side Sash Glazing=1.08 m²; Clearvue SHGC Value=0.683; Clearvue U Value=6.09; Custom Windload=1500 mm  [stored 4.92126 ft]; Custom Window Height=1790 mm  [stored 5.8727 ft]; Custom Window Width=2990 mm  [stored 9.80971 ft]; Energy Advantage SHGC Value=0.611; Energy Advantage U Value=4.53; Heavy Duty Handle=Yes; Heavy Duty Interlocker=Yes; Height=1790 mm  [stored 5.8727 ft]; Intruderprufe LowE SHGC Value=0.568; Intruderprufe LowE U Value=4.47; Intruderprufe SHGC Value=0.649; Intruderprufe U Value=5.97; Is Heavy Duty Handle=1 mm  [stored 0.00328084 ft]; Is Heavy Duty Mullion=1 mm  [stored 0.00328084 ft]; Limit Sash Width Side Max=1225 mm; Max Pane Area=1.08 m²; Sash Height=1733 mm; Sash Width Middle=762 mm; Sash Width Sides=762 mm; Standard Interlocker=No; Width=2990 mm  [stored 9.80971 ft]; Windload Design=1500 mm  [stored 4.92126 ft]
- 1000SW-3018XXXX-2000Pa: Area Middle Sash Glazing=1.08 m²; Area Side Sash Glazing=1.08 m²; Clearvue SHGC Value=0.683; Clearvue U Value=6.09; Custom Windload=2000 mm  [stored 6.56168 ft]; Custom Window Height=1790 mm  [stored 5.8727 ft]; Custom Window Width=2990 mm  [stored 9.80971 ft]; Energy Advantage SHGC Value=0.611; Energy Advantage U Value=4.53; Heavy Duty Handle=Yes; Heavy Duty Interlocker=Yes; Height=1790 mm  [stored 5.8727 ft]; Intruderprufe LowE SHGC Value=0.568; Intruderprufe LowE U Value=4.47; Intruderprufe SHGC Value=0.649; Intruderprufe U Value=5.97; Is Heavy Duty Handle=1 mm  [stored 0.00328084 ft]; Is Heavy Duty Mullion=1 mm  [stored 0.00328084 ft]; Limit Sash Width Side Max=1225 mm; Max Pane Area=1.08 m²; Sash Height=1733 mm; Sash Width Middle=762 mm; Sash Width Sides=762 mm; Standard Interlocker=No; Width=2990 mm  [stored 9.80971 ft]; Windload Design=2000 mm  [stored 6.56168 ft]
- 1000SW-2112XXXX-1500Pa: Area Middle Sash Glazing=0.45 m²; Area Side Sash Glazing=0.45 m²; Clearvue SHGC Value=0.612; Clearvue U Value=6.8; Custom Windload=1500 mm  [stored 4.92126 ft]; Custom Window Height=1190 mm  [stored 3.9042 ft]; Custom Window Width=2090 mm  [stored 6.85696 ft]; Energy Advantage SHGC Value=0.549; Energy Advantage U Value=4.87; Heavy Duty Handle=No; Heavy Duty Interlocker=No; Height=1190 mm  [stored 3.9042 ft]; Intruderprufe LowE SHGC Value=0.51; Intruderprufe LowE U Value=4.81; Intruderprufe SHGC Value=0.582; Intruderprufe U Value=6.07; Is Heavy Duty Handle=0 mm  [stored 0 ft]; Is Heavy Duty Mullion=0 mm  [stored 0 ft]; Limit Sash Width Side Max=775 mm; Max Pane Area=0.45 m²; Sash Height=1133 mm; Sash Width Middle=537 mm  [stored 1.76181 ft]; Sash Width Sides=537 mm  [stored 1.76181 ft]; Standard Interlocker=Yes; Width=2090 mm  [stored 6.85696 ft]; Windload Design=1500 mm  [stored 4.92126 ft]

note: [stored X ft] marks values corroborated as IEEE doubles in the binary element streams (Revit-internal decimal feet)

## geometry (parser evidence)
native form markers: Sweep x14
no freeform markers — native parametric forms only
